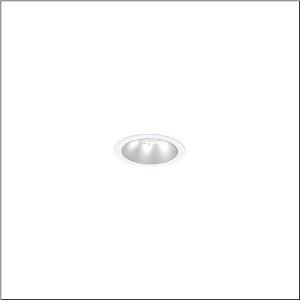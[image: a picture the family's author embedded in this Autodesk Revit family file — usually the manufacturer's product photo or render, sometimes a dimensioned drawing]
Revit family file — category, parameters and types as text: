
# Revit family: lunis_21_s_51db19ea91c
name_source: partatom
category: Lighting Fixtures
units: mm (PartAtom-declared; Revit-internal decimal feet)

## family parameters
Cut with Voids When Loaded = No
Host = Face
Light Source = No
Part Type = Normal
Room Calculation Point = No
Round Connector Dimension = Use Diameter
Shared = No

## types (1)
- --- (1 x LED, 1190 lm, 8 W, 6500K)
    Apparent Load = 8 VA
    CIE Flux Codes = 90 98 100 100 100
    Color Rendering = 80
    Color Temperature = 6500K
    Default Elevation = 1800 mm
    Description = Lunis 21,  S, downlight, light control with lens, of PMMA, anti glare with reflector, of PC, matt, light emission: direct distribution, LED rated luminous flux: 910lm, light colour: 830/840/865, with terminal, 5-pole, mains connection: 220..240V, AC, 50..60Hz, housing, round, of diecast aluminium, traffic white (RAL 9016), diameter: 84mm, clamping range: 1..40mm, protection rating (complete): IP20, protection rating (on room side): IP54, insulation class (complete): insulation class II (safety insulation), certification: CE, impact resistance: IK03, packaging unit: 1 piece
    Height = 0 mm  [stored 0 ft]
    Lamp = 1 x LED
    Lamp Light Flux = 1190 lm
    Lamp Power = 8 W
    Lamp count = 1
    Length = 84 mm
    Luminous efficacy = 149 lm/W
    Manufacturer = Siteco
    ModVariant = No
    Model = 51DB19EA91C
    Mounting Place = Ceiling
    Mounting Type = Recessed
    Number of Poles = 1
    OnlyDefault = Yes
    Power Factor = 1
    Product Name = Lunis 21 S
    Product group = downlight
    ProductGroupID = 401
    Protection Class = Protection class II
    Protection Degree = IP 20
    RLX_Detail_Level = 1
    RLX_Emergency_Light_Flux = 0 lm
    RLX_Emergency_Type = 0
    RLX_Emergency_Type_DB = No
    RlxData = <blob elided: 9613 chars, md5=8be11c73>
    Socket = socket
    Standby Power = 0 W
    System Light Flux = 1190 lm
    System Power = 8 W
    Type Comments = individual setting: colour temperature 6500K, luminous flux: 100 % | (OFF | OFF | ON | OFF) | 200 mA
    Type Image = l_1290846.jpg
    URL = http://relux.com
    VarID = @adj_039183
    Voltage = 0 V
    Weight = 0.00 kg
    Width = 0 mm  [stored 0 ft]

note: [stored X ft] marks values corroborated as IEEE doubles in the binary element streams (Revit-internal decimal feet)

## geometry (parser evidence)
native form markers: Sweep x11
no freeform markers — native parametric forms only
